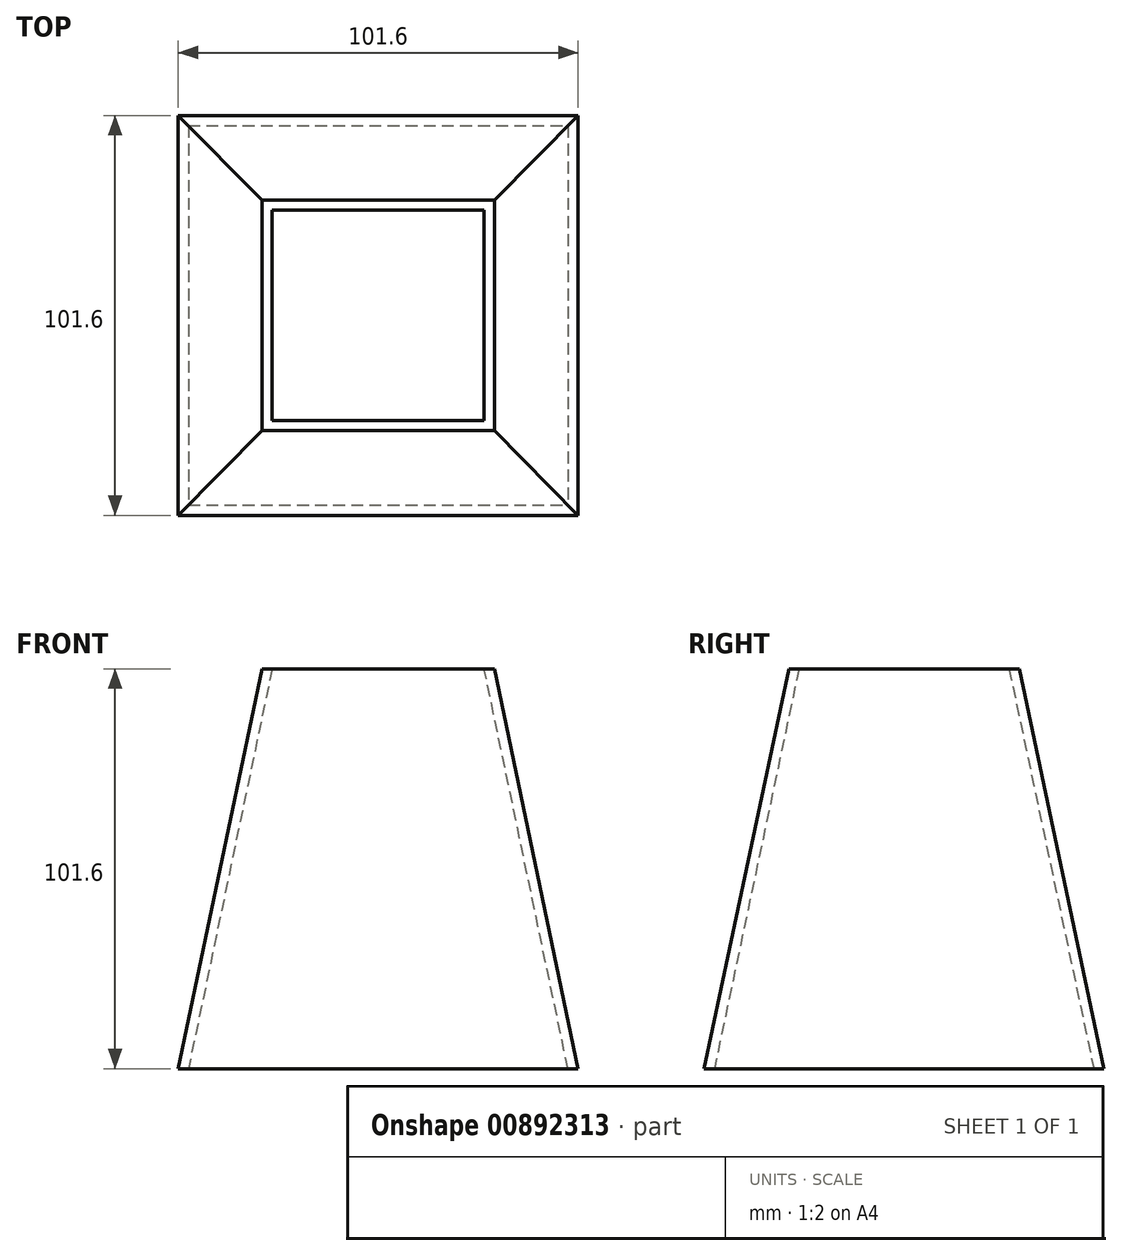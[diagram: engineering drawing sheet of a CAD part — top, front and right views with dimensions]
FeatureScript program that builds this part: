
annotation { "Feature Type Name" : "Feature", "Feature Type Description" : "" }
export const myFeature = defineFeature(function(context is Context, id is Id, definition is map)
    precondition{}
    {
        {
            var Q0;
            Q0=qCreatedBy(makeId("Top.planeOp"),FACE);
            var sketch = newSketch(context, id + "F0", { "sketchPlane" : qUnion([Q0])});
            skLineSegment(sketch, "E0.bottom", {"start": v(-50.8, 50.8) * mm, "end": v(50.8, 50.8) * mm});
            skLineSegment(sketch, "E0.top", {"start": v(-50.8, -50.8) * mm, "end": v(50.8, -50.8) * mm});
            skLineSegment(sketch, "E0.left", {"start": v(-50.8, 50.8) * mm, "end": v(-50.8, -50.8) * mm});
            skLineSegment(sketch, "E0.right", {"start": v(50.8, 50.8) * mm, "end": v(50.8, -50.8) * mm});
            skPoint(sketch, "E0.middle", {"position": v(0, 0) * mm});
            skSolve(sketch);
        }
        {
            var Q0;
            Q0=qCreatedBy(makeId("Top.planeOp"),FACE);
            cPlane(context, id + "F1", {"entities" : qUnion([Q0]), "cplaneType" : CPlaneType.OFFSET, "offset" : 101.6 * mm, "width" : 152.4 * mm, "height" : 152.4 * mm});
        }
        {
            var Q0;
            Q0=qCreatedBy(id+"F1.planeOp",FACE);
            var sketch = newSketch(context, id + "F2", { "sketchPlane" : qUnion([Q0])});
            skLineSegment(sketch, "E1.bottom", {"start": v(29.54, 29.3) * mm, "end": v(-29.54, 29.3) * mm});
            skLineSegment(sketch, "E1.top", {"start": v(29.54, -29.3) * mm, "end": v(-29.54, -29.3) * mm});
            skLineSegment(sketch, "E1.left", {"start": v(29.54, 29.3) * mm, "end": v(29.54, -29.3) * mm});
            skLineSegment(sketch, "E1.right", {"start": v(-29.54, 29.3) * mm, "end": v(-29.54, -29.3) * mm});
            skPoint(sketch, "E1.middle", {"position": v(0, 0) * mm});
            skSolve(sketch);
        }
        {
            var Q0;
            Q0 = qSketchRegion(id + "F0", true);
            var Q1;
            Q1 = qSketchRegion(id + "F2", true);
            loft(context, id + "F3", {"sheetProfilesArray" : [{ "sheetProfileEntities" : qUnion([Q0]) }, { "sheetProfileEntities" : qUnion([Q1]) }]});
        }
        {
            var Q0;
            Q0=makeQuery(id+"F3.opLoft","CAP_FACE",FACE,{"disambiguationData":[OSD([makeQuery(id+"F0.imprint","IMPRINT",FACE,{"disambiguationData":[TD([[makeQuery(id+"F0.imprint","IMPRINT",EDGE,{"derivedFrom":sQuery(id+"F0.wireOp",EDGE,"E0.bottom")}),-1.0]])]})])],"isStart":true});
            var Q1;
            Q1=makeQuery(id+"F3.opLoft","CAP_FACE",FACE,{"disambiguationData":[OSD([makeQuery(id+"F2.imprint","IMPRINT",FACE,{"disambiguationData":[TD([[makeQuery(id+"F2.imprint","IMPRINT",EDGE,{"derivedFrom":sQuery(id+"F2.wireOp",EDGE,"E1.bottom")}),1.0]])]})])],"isStart":true});
            var Q2;
            Q2=makeQuery(id+"F3.opLoft","SWEPT_BODY",BODY,{"disambiguationData":[OSD([makeQuery(id+"F0.imprint","IMPRINT",FACE,{"disambiguationData":[TD([[makeQuery(id+"F0.imprint","IMPRINT",EDGE,{"derivedFrom":sQuery(id+"F0.wireOp",EDGE,"E0.bottom")}),-1.0]])]}),makeQuery(id+"F2.imprint","IMPRINT",FACE,{"disambiguationData":[TD([[makeQuery(id+"F2.imprint","IMPRINT",EDGE,{"derivedFrom":sQuery(id+"F2.wireOp",EDGE,"E1.bottom")}),1.0]])]})])]});
            shell(context, id + "F4", {"entities" : qUnion([Q0, Q1]), "parts" : qUnion([Q2]), "thickness" : 2.54 * mm});
        }
    });
